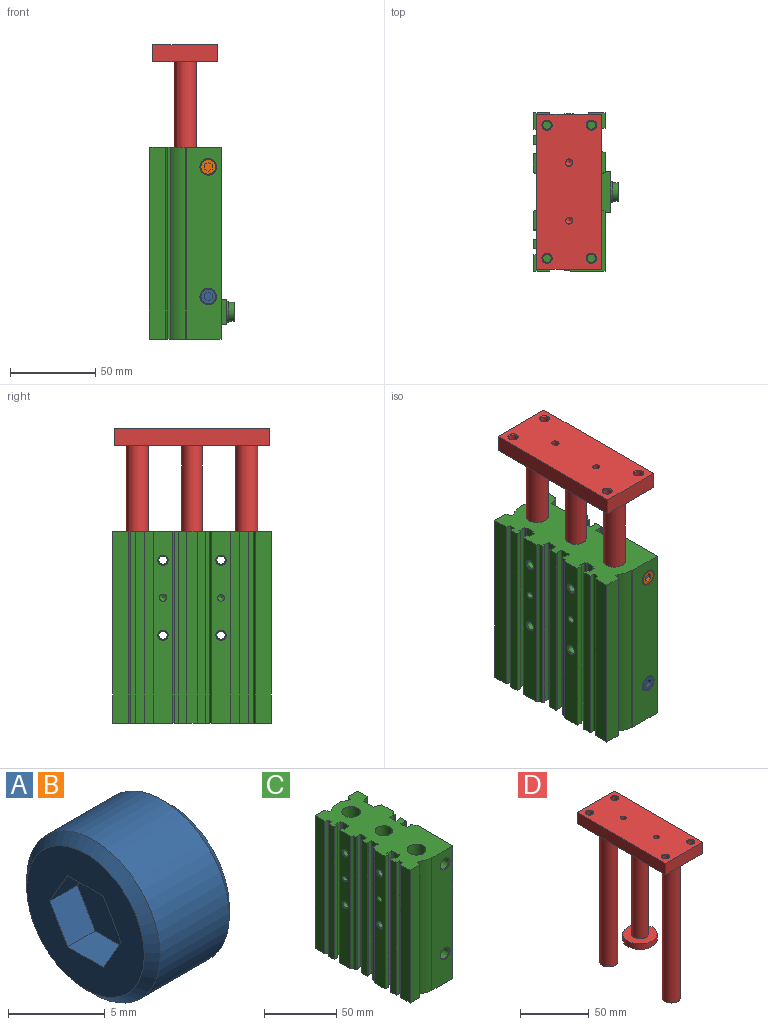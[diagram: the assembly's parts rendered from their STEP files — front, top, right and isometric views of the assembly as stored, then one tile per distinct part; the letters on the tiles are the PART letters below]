
ASSEMBLY  parts=4 mates=3
PART A: 12 faces, bbox 6.2x9.7x9.7 mm
  f0: cone r=4.28mm half-angle=45deg, axis (1,0,0), area 23.6mm2, adj f1,f7
  f1: plane 8.57x8.57mm, normal (-1,0,0), area 40.1mm2, adj f0,f2,f3,f4,f8,f9,f10
  f2: plane 2.25x2mm, normal (0,0.87,-0.5), area 5.2mm2, adj f1,f3,f4,f11
  f3: plane 2.25x2mm, normal (0,0.87,0.5), area 5.2mm2, adj f1,f2,f8,f11
  f4: plane 2.6x2mm, normal (0,0,-1), area 5.2mm2, adj f1,f2,f10,f11
  f5: plane 8.57x8.57mm, normal (1,0,0), area 57.6mm2, adj f6
  f6: cone r=4.86mm half-angle=45deg, axis (-1,0,0), area 23.6mm2, adj f5,f7
  f7: cylinder r=4.86mm len=9.73mm, axis (-1,0,0), area 154mm2, adj f0,f6
  f8: plane 2.6x2mm, normal (0,0,1), area 5.2mm2, adj f1,f3,f9,f11
  f9: plane 2.25x2mm, normal (0,-0.87,0.5), area 5.2mm2, adj f1,f8,f10,f11
  f10: plane 2.25x2mm, normal (0,-0.87,-0.5), area 5.2mm2, adj f1,f4,f9,f11
  f11: plane 5.2x4.5mm, normal (-1,0,0), area 17.5mm2, adj f2,f3,f4,f8,f9,f10
PART B: same geometry as A
PART C: 197 faces, bbox 50x93x112.5 mm
  f0: plane 8.5x3.7mm, normal (0,1,0), area 31.5mm2, adj f1,f2,f117,f169
  f1: plane 8.5x0.63mm, normal (-0.87,0.5,0), area 6.1mm2, adj f0,f117,f161,f169
  f2: plane 8.5x6.3mm, normal (1,0,0), area 53.6mm2, adj f0,f117,f167,f169
  f3: plane 89x3.7mm, normal (0,1,0), area 329.3mm2, adj f118,f168,f192,f193
  f4: plane 112.5x11.46mm, normal (1,0,0), area 1140.6mm2, adj f10,f13,f87,f105,f117,f118,f168,f169
  f5: plane 112.5x34.96mm, normal (1,0,0), area 3635.7mm2, adj f8,f11,f81,f84,f93,f99,f117,f118
  f6: plane 112.5x9mm, normal (1,0,0), area 1012.5mm2, adj f9,f117,f118,f126
  f7: plane 112.5x10.76mm, normal (-1,0,0), area 1139.4mm2, adj f43,f67,f68,f69,f70,f92,f110,f117
  f8: plane 112.5x20.5mm, normal (0,-1,0), area 2157.6mm2, adj f5,f15,f75,f78,f117,f118
  f9: plane 112.5x6mm, normal (0.34,-0.94,0), area 718.3mm2, adj f6,f12,f117,f118
  f10: plane 112.5x6mm, normal (0.34,0.94,0), area 718.3mm2, adj f4,f12,f117,f118
  f11: plane 8.5x1.8mm, normal (0.5,0.87,0), area 17.7mm2, adj f5,f117,f120,f169
  f12: plane 112.5x10.13mm, normal (1,0,0), area 1139.9mm2, adj f9,f10,f117,f118
  f13: plane 8.5x1.8mm, normal (0.5,-0.87,0), area 17.7mm2, adj f4,f14,f117,f169
  f14: plane 8.5x2.48mm, normal (1,0,0), area 21mm2, adj f13,f117,f163,f169
  f15: plane 112.5x0.5mm, normal (-0.94,-0.34,0), area 60.3mm2, adj f8,f16,f117,f118
  f16: cylinder r=14mm len=112.5mm, axis (0,0,1), area 1086.1mm2, adj f15,f17,f117,f118
  f17: plane 112.5x1.57mm, normal (0,-1,0), area 176.2mm2, adj f16,f18,f117,f118
  f18: plane 112.5x3.5mm, normal (0.94,-0.34,0), area 419mm2, adj f17,f117,f118,f127
  f19: plane 112.5x9.5mm, normal (-1,0,0), area 1068.8mm2, adj f20,f117,f118,f127
  f20: plane 112.5x2.7mm, normal (-0.34,0.94,0), area 323.2mm2, adj f19,f21,f117,f118
  f21: plane 112.5x3.02mm, normal (-1,0,0), area 339.4mm2, adj f20,f22,f117,f118
  f22: plane 112.5x3mm, normal (0,-1,0), area 337.5mm2, adj f21,f117,f118,f196
  f23: plane 112.5x1.5mm, normal (1,0,0), area 168.8mm2, adj f24,f33,f117,f118
  f24: plane 112.5x4.5mm, normal (0,-1,0), area 506.2mm2, adj f23,f25,f117,f118
  f25: plane 112.5x1.5mm, normal (-1,0,0), area 168.8mm2, adj f24,f26,f117,f118
  f26: plane 112.5x0.7mm, normal (0,-1,0), area 78.7mm2, adj f25,f27,f117,f118
  f27: plane 112.5x5.4mm, normal (-1,0,0), area 607.5mm2, adj f26,f28,f117,f118
  f28: plane 112.5x0.7mm, normal (0,1,0), area 78.7mm2, adj f27,f29,f117,f118
  f29: plane 112.5x1.5mm, normal (-1,0,0), area 168.8mm2, adj f28,f30,f117,f118
  f30: plane 112.5x4.5mm, normal (0,1,0), area 506.2mm2, adj f29,f31,f117,f118
  f31: plane 112.5x1.5mm, normal (1,0,0), area 168.8mm2, adj f30,f32,f117,f118
  f32: plane 112.5x3mm, normal (0,1,0), area 337.5mm2, adj f31,f117,f118,f196
  f33: plane 112.5x3mm, normal (0,-1,0), area 337.5mm2, adj f23,f117,f118,f124
  f34: plane 112.5x1.5mm, normal (1,0,0), area 168.8mm2, adj f35,f44,f117,f118
  f35: plane 112.5x4.5mm, normal (0,-1,0), area 506.2mm2, adj f34,f36,f117,f118
  f36: plane 112.5x1.5mm, normal (-1,0,0), area 168.8mm2, adj f35,f37,f117,f118
  f37: plane 112.5x0.7mm, normal (0,-1,0), area 78.7mm2, adj f36,f38,f117,f118
  f38: plane 112.5x5.4mm, normal (-1,0,0), area 607.5mm2, adj f37,f39,f117,f118
  f39: plane 112.5x0.7mm, normal (0,1,0), area 78.7mm2, adj f38,f40,f117,f118
  f40: plane 112.5x1.5mm, normal (-1,0,0), area 168.8mm2, adj f39,f41,f117,f118
  f41: plane 112.5x4.5mm, normal (0,1,0), area 506.2mm2, adj f40,f42,f117,f118
  f42: plane 112.5x1.5mm, normal (1,0,0), area 168.8mm2, adj f41,f43,f117,f118
  f43: plane 112.5x3mm, normal (0,1,0), area 337.5mm2, adj f7,f42,f117,f118
  f44: plane 112.5x3mm, normal (0,-1,0), area 337.5mm2, adj f34,f117,f118,f128
  f45: plane 4x2.25mm, normal (0,0,-1), area 1mm2, adj f46,f47,f48,f50
  f46: plane 3x0.5mm, normal (-1,0,0), area 1.5mm2, adj f45,f47,f49,f117,f195
  f47: cylinder r=2mm len=4mm, axis (0,0,1), area 18.8mm2, adj f45,f46,f48,f117
  f48: plane 3x0.5mm, normal (1,0,0), area 1.5mm2, adj f45,f47,f49,f117,f195
  f49: cylinder r=2mm len=4mm, axis (0,0,1), area 18.8mm2, adj f46,f48,f117,f195
  f50: cylinder r=2mm len=4mm, axis (0,0,1), area 37.7mm2, adj f45,f51,f195
  f51: cone r=866.03mm half-angle=60deg, axis (0,0,-1), area 14.5mm2, adj f50
  f52: cylinder r=2mm len=6mm, axis (0,0,1), area 75.4mm2, adj f53,f117
  f53: cone r=866.03mm half-angle=60deg, axis (0,0,-1), area 14.5mm2, adj f52
  f54: cone r=2.46mm half-angle=45deg, axis (0,0,-1), area 13.1mm2, adj f55,f117
  f55: cylinder r=2.46mm len=14.46mm, axis (0,0,1), area 223.3mm2, adj f54,f56
  f56: plane 4.92x4.92mm, normal (0,0,-1), area 19mm2, adj f55
  f57: cone r=2.46mm half-angle=45deg, axis (0,0,-1), area 13.1mm2, adj f58,f117
  f58: cylinder r=2.46mm len=14.46mm, axis (0,0,1), area 223.3mm2, adj f57,f59
  f59: plane 4.92x4.92mm, normal (0,0,-1), area 19mm2, adj f58
  f60: cone r=2.46mm half-angle=45deg, axis (0,0,-1), area 13.1mm2, adj f61,f117
  f61: cylinder r=2.46mm len=14.46mm, axis (0,0,1), area 223.3mm2, adj f60,f62
  f62: plane 4.92x4.92mm, normal (0,0,-1), area 19mm2, adj f61
  f63: cone r=2.46mm half-angle=45deg, axis (0,0,-1), area 13.1mm2, adj f64,f117
  f64: cylinder r=2.46mm len=14.46mm, axis (0,0,1), area 223.3mm2, adj f63,f65
  f65: plane 4.92x4.92mm, normal (0,0,-1), area 19mm2, adj f64
  f66: plane 4x2.25mm, normal (-1,0,0), area 1mm2, adj f67,f68,f69,f72
  f67: plane 3x0.5mm, normal (0,0,1), area 1.5mm2, adj f7,f66,f68,f70,f194
  f68: cylinder r=2mm len=4mm, axis (1,0,0), area 18.8mm2, adj f7,f66,f67,f69
  f69: plane 3x0.5mm, normal (0,0,-1), area 1.5mm2, adj f7,f66,f68,f70,f194
  f70: cylinder r=2mm len=4mm, axis (1,0,0), area 18.8mm2, adj f7,f67,f69,f194
  f71: cone r=2mm half-angle=60deg, axis (-1,0,0), area 14.5mm2, adj f72
  f72: cylinder r=2mm len=4mm, axis (-1,0,0), area 37.7mm2, adj f66,f71,f194
  f73: cone r=2mm half-angle=60deg, axis (-1,0,0), area 14.5mm2, adj f74
  f74: cylinder r=2mm len=6mm, axis (-1,0,0), area 75.4mm2, adj f73,f124
  f75: cone r=4.28mm half-angle=45deg, axis (0,-1,0), area 23.6mm2, adj f8,f76
  f76: cylinder r=4.28mm len=8.57mm, axis (0,1,0), area 199.7mm2, adj f75,f77
  f77: cone r=866.03mm half-angle=60deg, axis (0,-1,0), area 66.5mm2, adj f76
  f78: cone r=4.28mm half-angle=45deg, axis (0,-1,0), area 23.6mm2, adj f8,f79
  f79: cylinder r=4.28mm len=8.57mm, axis (0,1,0), area 199.7mm2, adj f78,f80
  f80: cone r=866.03mm half-angle=60deg, axis (0,-1,0), area 66.5mm2, adj f79
  f81: cone r=4.28mm half-angle=45deg, axis (1,0,0), area 23.6mm2, adj f5,f82
  f82: cylinder r=4.28mm len=9.42mm, axis (-1,0,0), area 253.5mm2, adj f81,f83
  f83: cone r=866.03mm half-angle=60deg, axis (1,0,0), area 66.5mm2, adj f82
  f84: cone r=4.28mm half-angle=45deg, axis (1,0,0), area 23.6mm2, adj f5,f85
  f85: cylinder r=4.28mm len=9.42mm, axis (-1,0,0), area 253.5mm2, adj f84,f86
  f86: cone r=866.03mm half-angle=60deg, axis (1,0,0), area 66.5mm2, adj f85
  f87: cylinder r=4.75mm len=9.5mm, axis (-1,0,0), area 164.1mm2, adj f4,f88
  f88: plane 9.5x9.5mm, normal (1,0,0), area 48mm2, adj f87,f89
  f89: cylinder r=2.7mm len=24.5mm, axis (-1,0,0), area 415.6mm2, adj f88,f90
  f90: plane 5.4x5.4mm, normal (1,0,0), area 3.9mm2, adj f89,f91
  f91: cylinder r=2.46mm len=11.46mm, axis (-1,0,0), area 177mm2, adj f90,f92
  f92: cone r=3mm half-angle=45deg, axis (-1,0,0), area 13.1mm2, adj f7,f91
  f93: cylinder r=4.75mm len=9.5mm, axis (-1,0,0), area 164.1mm2, adj f5,f94
  f94: plane 9.5x9.5mm, normal (1,0,0), area 48mm2, adj f93,f95
  f95: cylinder r=2.7mm len=24.5mm, axis (-1,0,0), area 415.6mm2, adj f94,f96
  f96: plane 5.4x5.4mm, normal (1,0,0), area 3.9mm2, adj f95,f97
  f97: cylinder r=2.46mm len=11.46mm, axis (-1,0,0), area 177mm2, adj f96,f98
  f98: cone r=3mm half-angle=45deg, axis (-1,0,0), area 13.1mm2, adj f97,f124
  f99: cylinder r=4.75mm len=9.5mm, axis (-1,0,0), area 164.1mm2, adj f5,f100
  f100: plane 9.5x9.5mm, normal (1,0,0), area 48mm2, adj f99,f101
  f101: cylinder r=2.7mm len=24.5mm, axis (-1,0,0), area 415.6mm2, adj f100,f102
  f102: plane 5.4x5.4mm, normal (1,0,0), area 3.9mm2, adj f101,f103
  f103: cylinder r=2.46mm len=11.46mm, axis (-1,0,0), area 177mm2, adj f102,f104
  f104: cone r=3mm half-angle=45deg, axis (-1,0,0), area 13.1mm2, adj f103,f124
  f105: cylinder r=4.75mm len=9.5mm, axis (-1,0,0), area 164.1mm2, adj f4,f106
  f106: plane 9.5x9.5mm, normal (1,0,0), area 48mm2, adj f105,f107
  f107: cylinder r=2.7mm len=24.5mm, axis (-1,0,0), area 415.6mm2, adj f106,f108
  f108: plane 5.4x5.4mm, normal (1,0,0), area 3.9mm2, adj f107,f109
  f109: cylinder r=2.46mm len=11.46mm, axis (-1,0,0), area 177mm2, adj f108,f110
  f110: cone r=3mm half-angle=45deg, axis (-1,0,0), area 13.1mm2, adj f7,f109
  f111: plane 25x25mm, normal (0,0,1), area 490.9mm2, adj f113
  f112: plane 25x25mm, normal (0,0,-1), area 377.8mm2, adj f113,f114
  f113: cylinder r=12.5mm len=55mm, axis (0,0,-1), area 4319.7mm2, adj f111,f112
  f114: cylinder r=6mm len=28.75mm, axis (0,0,-1), area 1083.8mm2, adj f112,f118
  f115: cylinder r=6.5mm len=112.5mm, axis (0,0,-1), area 4594.6mm2, adj f117,f118
  f116: cylinder r=6.5mm len=112.5mm, axis (0,0,-1), area 4594.6mm2, adj f117,f118
  f117: plane 93x42mm, normal (0,0,-1), area 3023mm2, adj f0,f1,f2,f4,f5,f6,f7,f8
  f118: plane 93x42mm, normal (0,0,1), area 3050.1mm2, adj f3,f4,f5,f6,f7,f8,f9,f10
  f119: plane 8.5x5.95mm, normal (1,0,0), area 50.6mm2, adj f117,f160,f161,f169
  f120: plane 8.5x2.48mm, normal (1,0,0), area 21mm2, adj f11,f117,f154,f169
  f121: plane 112.5x2.48mm, normal (-1,0,0), area 278.5mm2, adj f117,f118,f129,f143
  f122: plane 112.5x5.95mm, normal (-1,0,0), area 669.4mm2, adj f117,f118,f135,f136
  f123: plane 112.5x2.48mm, normal (-1,0,0), area 278.5mm2, adj f117,f118,f142,f144
  f124: plane 112.5x10.76mm, normal (-1,0,0), area 1141.4mm2, adj f33,f74,f98,f104,f117,f118,f143
  f125: plane 112.5x9.2mm, normal (0,1,0), area 1035mm2, adj f117,f118,f148,f149
  f126: plane 112.5x9.5mm, normal (0,1,0), area 1068.8mm2, adj f6,f117,f118,f153
  f127: plane 112.5x9.2mm, normal (0,-1,0), area 1035mm2, adj f18,f19,f117,f118
  f128: plane 112.5x5.3mm, normal (-1,0,0), area 596.3mm2, adj f44,f117,f118,f145
  f129: plane 112.5x0.94mm, normal (0,1,0), area 105.7mm2, adj f117,f118,f121,f130
  f130: plane 112.5x0.63mm, normal (0.87,0.5,0), area 81.2mm2, adj f117,f118,f129,f131
  f131: plane 112.5x3.7mm, normal (0,1,0), area 416.2mm2, adj f117,f118,f130,f132
  f132: plane 112.5x6.3mm, normal (-1,0,0), area 708.8mm2, adj f117,f118,f131,f133
  f133: plane 112.5x3.7mm, normal (0,-1,0), area 416.2mm2, adj f117,f118,f132,f134
  f134: plane 112.5x0.63mm, normal (0.87,-0.5,0), area 81.2mm2, adj f117,f118,f133,f135
  f135: plane 112.5x0.94mm, normal (0,-1,0), area 105.7mm2, adj f117,f118,f122,f134
  f136: plane 112.5x0.94mm, normal (0,1,0), area 105.7mm2, adj f117,f118,f122,f137
  f137: plane 112.5x0.63mm, normal (0.87,0.5,0), area 81.2mm2, adj f117,f118,f136,f138
  f138: plane 112.5x3.7mm, normal (0,1,0), area 416.2mm2, adj f117,f118,f137,f139
  f139: plane 112.5x6.3mm, normal (-1,0,0), area 708.8mm2, adj f117,f118,f138,f140
  f140: plane 112.5x3.7mm, normal (0,-1,0), area 416.2mm2, adj f117,f118,f139,f141
  f141: plane 112.5x0.63mm, normal (0.87,-0.5,0), area 81.2mm2, adj f117,f118,f140,f142
  f142: plane 112.5x0.94mm, normal (0,-1,0), area 105.7mm2, adj f117,f118,f123,f141
  f143: plane 112.5x1.8mm, normal (-0.5,0.87,0), area 233.8mm2, adj f117,f118,f121,f124
  f144: plane 112.5x1.8mm, normal (-0.5,-0.87,0), area 233.8mm2, adj f7,f117,f118,f123
  f145: plane 112.5x3mm, normal (0,1,0), area 337.5mm2, adj f117,f118,f128,f146
  f146: plane 112.5x3.02mm, normal (-1,0,0), area 339.4mm2, adj f117,f118,f145,f147
  f147: plane 112.5x2.7mm, normal (-0.34,-0.94,0), area 323.2mm2, adj f117,f118,f146,f148
  f148: plane 112.5x9.5mm, normal (-1,0,0), area 1068.8mm2, adj f117,f118,f125,f147
  f149: plane 112.5x3.5mm, normal (0.94,0.34,0), area 419mm2, adj f117,f118,f125,f150
  f150: plane 112.5x1.57mm, normal (0,1,0), area 176.2mm2, adj f117,f118,f149,f151
  f151: cylinder r=14mm len=112.5mm, axis (0,0,1), area 2100.9mm2, adj f117,f118,f150,f152
  f152: plane 112.5x1.57mm, normal (0,1,0), area 176.2mm2, adj f117,f118,f151,f153
  f153: plane 112.5x3.5mm, normal (-0.94,0.34,0), area 419mm2, adj f117,f118,f126,f152
  f154: plane 8.5x0.94mm, normal (0,1,0), area 8mm2, adj f117,f120,f155,f169
  f155: plane 8.5x0.63mm, normal (-0.87,0.5,0), area 6.1mm2, adj f117,f154,f156,f169
  f156: plane 8.5x3.7mm, normal (0,1,0), area 31.5mm2, adj f117,f155,f157,f169
  f157: plane 8.5x6.3mm, normal (1,0,0), area 53.6mm2, adj f117,f156,f158,f169
  f158: plane 8.5x3.7mm, normal (0,-1,0), area 31.5mm2, adj f117,f157,f159,f169
  f159: plane 8.5x0.63mm, normal (-0.87,-0.5,0), area 6.1mm2, adj f117,f158,f160,f169
  f160: plane 8.5x0.94mm, normal (0,-1,0), area 8mm2, adj f117,f119,f159,f169
  f161: plane 8.5x0.94mm, normal (0,1,0), area 8mm2, adj f1,f117,f119,f169
  f162: plane 8.5x0.63mm, normal (-0.87,-0.5,0), area 6.1mm2, adj f117,f163,f167,f169
  f163: plane 8.5x0.94mm, normal (0,-1,0), area 8mm2, adj f14,f117,f162,f169
  f164: plane 89x0.94mm, normal (0,1,0), area 83.6mm2, adj f118,f168,f189,f192
  f165: plane 89x0.63mm, normal (-0.87,-0.5,0), area 64.2mm2, adj f118,f166,f168,f191
  f166: plane 89x3.7mm, normal (0,-1,0), area 329.3mm2, adj f118,f165,f168,f193
  f167: plane 8.5x3.7mm, normal (0,-1,0), area 31.5mm2, adj f2,f117,f162,f169
  f168: plane 24x10.3mm, normal (0,0,1), area 183.9mm2, adj f3,f4,f5,f164,f165,f166,f170,f171
  f169: plane 24x10.3mm, normal (0,0,-1), area 183.9mm2, adj f0,f1,f2,f4,f5,f11,f13,f14
  f170: plane 15x3.5mm, normal (0,1,0), area 52.5mm2, adj f4,f168,f169,f172
  f171: plane 15x3.5mm, normal (0,-1,0), area 52.5mm2, adj f5,f168,f169,f172
  f172: plane 24x15mm, normal (1,0,0), area 237.3mm2, adj f168,f169,f170,f171,f173
  f173: cylinder r=6.25mm len=12.5mm, axis (-1,0,0), area 39.3mm2, adj f172,f174
  f174: plane 12.5x12.5mm, normal (1,0,0), area 27.7mm2, adj f173,f175
  f175: cylinder r=5.5mm len=11mm, axis (-1,0,0), area 110.6mm2, adj f174,f176
  f176: plane 11x11mm, normal (1,0,0), area 71.3mm2, adj f175,f177
  f177: cylinder r=2.75mm len=5.5mm, axis (-1,0,0), area 5.2mm2, adj f176,f178
  f178: plane 5.5x5.5mm, normal (1,0,0), area 23.8mm2, adj f177
  f179: plane 89x0.94mm, normal (0,-1,0), area 83.6mm2, adj f118,f168,f180,f189
  f180: plane 89x0.63mm, normal (-0.87,-0.5,0), area 64.2mm2, adj f118,f168,f179,f181
  f181: plane 89x3.7mm, normal (0,-1,0), area 329.3mm2, adj f118,f168,f180,f182
  f182: plane 89x6.3mm, normal (1,0,0), area 560.7mm2, adj f118,f168,f181,f183
  f183: plane 89x3.7mm, normal (0,1,0), area 329.3mm2, adj f118,f168,f182,f184
  f184: plane 89x0.63mm, normal (-0.87,0.5,0), area 64.2mm2, adj f118,f168,f183,f185
  f185: plane 89x0.94mm, normal (0,1,0), area 83.6mm2, adj f118,f168,f184,f188
  f186: plane 89x1.8mm, normal (0.5,0.87,0), area 185mm2, adj f5,f118,f168,f188
  f187: plane 89x1.8mm, normal (0.5,-0.87,0), area 185mm2, adj f4,f118,f168,f190
  f188: plane 89x2.48mm, normal (1,0,0), area 220.3mm2, adj f118,f168,f185,f186
  f189: plane 89x5.95mm, normal (1,0,0), area 529.6mm2, adj f118,f164,f168,f179
  f190: plane 89x2.48mm, normal (1,0,0), area 220.3mm2, adj f118,f168,f187,f191
  f191: plane 89x0.94mm, normal (0,-1,0), area 83.6mm2, adj f118,f165,f168,f190
  f192: plane 89x0.63mm, normal (-0.87,0.5,0), area 64.2mm2, adj f3,f118,f164,f168
  f193: plane 89x6.3mm, normal (1,0,0), area 560.7mm2, adj f3,f118,f166,f168
  f194: plane 4x2.25mm, normal (-1,0,0), area 1mm2, adj f67,f69,f70,f72
  f195: plane 4x2.25mm, normal (0,0,-1), area 1mm2, adj f46,f48,f49,f50
  f196: plane 112.5x5.3mm, normal (-1,0,0), area 596.2mm2, adj f22,f32,f117,f118
PART D: 36 faces, bbox 38x91x135.5 mm
  f0: cylinder r=2mm len=4mm, axis (0,0,1), area 37.7mm2, adj f2,f27,f35
  f1: cylinder r=6.5mm len=125.5mm, axis (0,0,-1), area 5125.5mm2, adj f5,f28
  f2: cone r=2mm half-angle=60deg, axis (0,0,1), area 14.5mm2, adj f0
  f3: plane 38x10mm, normal (0,1,0), area 380mm2, adj f4,f5,f6,f7
  f4: plane 91x10mm, normal (-1,0,0), area 910mm2, adj f3,f5,f6,f8
  f5: plane 91x38mm, normal (0,0,-1), area 2966.3mm2, adj f1,f3,f4,f7,f8,f11,f14,f17
  f6: plane 91x38mm, normal (0,0,1), area 3317.8mm2, adj f3,f4,f7,f8,f9,f12,f15,f18
  f7: plane 91x10mm, normal (1,0,0), area 910mm2, adj f3,f5,f6,f8
  f8: plane 38x10mm, normal (0,-1,0), area 380mm2, adj f4,f5,f6,f7
  f9: cone r=3mm half-angle=45deg, axis (0,0,1), area 13.1mm2, adj f6,f10
  f10: cylinder r=2.46mm len=8.92mm, axis (0,0,1), area 137.7mm2, adj f9,f11
  f11: cone r=2.46mm half-angle=45deg, axis (0,0,-1), area 13.1mm2, adj f5,f10
  f12: cone r=3mm half-angle=45deg, axis (0,0,1), area 13.1mm2, adj f6,f13
  f13: cylinder r=2.46mm len=8.92mm, axis (0,0,1), area 137.7mm2, adj f12,f14
  f14: cone r=2.46mm half-angle=45deg, axis (0,0,-1), area 13.1mm2, adj f5,f13
  f15: cone r=3mm half-angle=45deg, axis (0,0,1), area 13.1mm2, adj f6,f16
  f16: cylinder r=2.46mm len=8.92mm, axis (0,0,1), area 137.7mm2, adj f15,f17
  f17: cone r=2.46mm half-angle=45deg, axis (0,0,-1), area 13.1mm2, adj f5,f16
  f18: cone r=3mm half-angle=45deg, axis (0,0,1), area 13.1mm2, adj f6,f19
  f19: cylinder r=2.46mm len=8.92mm, axis (0,0,1), area 137.7mm2, adj f18,f20
  f20: cone r=2.46mm half-angle=45deg, axis (0,0,-1), area 13.1mm2, adj f5,f19
  f21: cylinder r=2mm len=6mm, axis (0,0,1), area 75.4mm2, adj f6,f22
  f22: cone r=2mm half-angle=60deg, axis (0,0,1), area 14.5mm2, adj f21
  f23: cylinder r=2mm len=4mm, axis (0,0,-1), area 18.8mm2, adj f6,f24,f26,f35
  f24: plane 3x0.5mm, normal (1,0,0), area 1.5mm2, adj f6,f23,f25,f27,f35
  f25: cylinder r=2mm len=4mm, axis (0,0,-1), area 18.8mm2, adj f6,f24,f26,f27
  f26: plane 3x0.5mm, normal (-1,0,0), area 1.5mm2, adj f6,f23,f25,f27,f35
  f27: plane 4x2.25mm, normal (0,0,1), area 1mm2, adj f0,f24,f25,f26
  f28: plane 13x13mm, normal (0,0,-1), area 132.7mm2, adj f1
  f29: cylinder r=6.5mm len=125.5mm, axis (0,0,-1), area 5125.5mm2, adj f5,f30
  f30: plane 13x13mm, normal (0,0,-1), area 132.7mm2, adj f29
  f31: cylinder r=6mm len=84.75mm, axis (0,0,-1), area 3195mm2, adj f5,f34
  f32: cylinder r=12.5mm len=25mm, axis (0,0,1), area 392.7mm2, adj f33,f34
  f33: plane 25x25mm, normal (0,0,-1), area 490.9mm2, adj f32
  f34: plane 25x25mm, normal (0,0,1), area 377.8mm2, adj f31,f32
  f35: plane 4x2.25mm, normal (0,0,1), area 1mm2, adj f0,f23,f24,f26
PLACE A rot(axis=(-0.58,-0.58,0.58),120deg) t=(-53.9,-8.78,-154.01)mm
PLACE B rot(axis=(-0.58,-0.58,0.58),120deg) t=(-53.9,-8.78,-78.01)mm
PLACE C t=(-67.4,37.72,-66.51)mm fixed
PLACE D t=(-67.4,37.72,-6.51)mm
MATE fastened C.f78 <-> B.f0  axis (0,-1,0) through (-53.9,-8.2,-78.01)mm
MATE slider C.f113 <-> D.f31  axis (0,0,1) through (-67.4,37.72,-66.51)mm
MATE fastened C.f75 <-> A.f0  axis (0,-1,0) through (-53.9,-8.2,-154.01)mm
